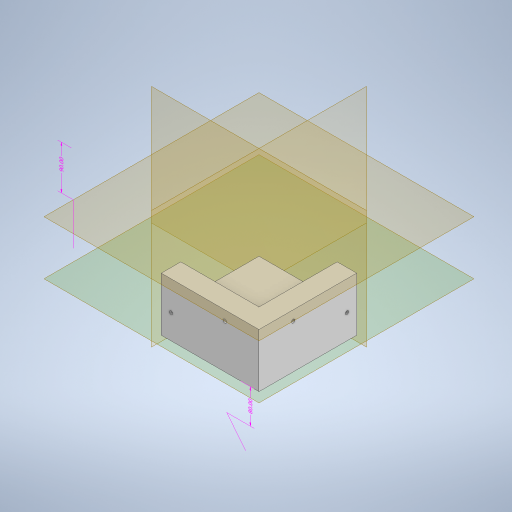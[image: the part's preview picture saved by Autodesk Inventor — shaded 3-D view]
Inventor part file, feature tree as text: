
AUTODESK INVENTOR PART (.ipt)
format: ipt  version: 2023 (Build 270158000, 158)  size: 429,568 bytes
history: native  units: mm
features: sketch x9, extrude x5, other x4, hole x4, plane x4, split x4
ambient origin geometry x8: Origin, YZ Plane, XZ Plane, XY Plane, X Axis, Y Axis, Z Axis, Center Point
bodies: Body1 (feature_tree)
feature tree (30):
  other  "Sólido1"
  other  "Anotaciones"
  extrude  "Extrusión1"  Depth=200.0mm
  hole  "Agujero1"  [1 undecoded]
  extrude  "Extrusión2"  Depth=15.0mm
  extrude  "Extrusión3"  Depth=80.0mm TaperAngle=0.0deg
  extrude  "Extrusión4"  Depth=200.0mm
  extrude  "Extrusión5"  Depth=20.0mm
  hole  "Agujero2"  [1 undecoded]
  plane  "Plano de trabajo1"
  split  "Dividir1"
  plane  "Plano de trabajo2"
  plane  "Plano de trabajo3"
  sketch  "Boceto9"  dims[d37=20.0mm d38=20.0mm]
  plane  "Plano de trabajo4"
  hole  "Agujero3"  [1 undecoded]
  hole  "Agujero4"  [1 undecoded]
  split  "Dividir2"
  split  "Dividir3"
  split  "Dividir4"
  sketch  "Boceto2"  dims[d7=15.0mm d8=200.0mm]
  sketch  "Boceto3"  dims[d9=10.0mm d10=0.0mm]
  sketch  "Boceto4"  dims[d12=1.75mm d13=1.75mm d14=1.75mm d15=1.75mm d16=10.0mm d17=10.0mm d19=30.0mm]
  sketch  "Boceto5"  dims[d20=3.5mm d21=6.0mm d22=4.0mm d23=2.0mm d24=90.0deg d25=8.0mm d26=20.594885mm d27=15.0mm]
  sketch  "Boceto6"  dims[d28=20.0mm d29=80.0mm d30=0.0mm]
  sketch  "Boceto7"  dims[d31=48.0mm d32=200.0mm]
  sketch  "Boceto8"  dims[d33=110.0mm d34=0.0mm d36=20.0mm]
  sketch  "Boceto10"  dims[d39=90.0mm d40=0.0mm d42=10.0mm d43=30.0mm d44=0.0mm d46=1.75mm d47=1.75mm d48=1.75mm d49=1.75mm d50=10.0mm d51=10.0mm d52=15.0mm d56=3.5mm d57=6.0mm d58=4.0mm d59=2.0mm d60=90.0deg d61=8.0mm d62=20.594885mm d63=10.0mm d65=10.0mm d66=10.0mm d67=31.75mm d70=15.0mm d74=200.0mm d78=20.0mm d82=90.0deg d83=10.0mm d84=30.0mm d85=5.0mm d86=5.0mm d87=5.0mm d88=5.0mm d89=20.0mm d91=30.0mm d92=5.0mm d93=5.0mm d94=3.5mm d95=5.0mm d96=5.0mm d97=5.0mm d98=5.0mm d99=5.0mm d100=20.0mm d101=3.5mm d102=6.0mm d103=4.0mm d104=2.0mm d105=90.0deg d106=8.0mm d107=20.594885mm d108=10.0mm d109=30.0mm d110=5.0mm d111=5.0mm d112=5.0mm d113=5.0mm d114=5.0mm d115=5.0mm d116=3.5mm d117=5.0mm d118=5.0mm d119=5.0mm d120=5.0mm d121=5.0mm d122=30.0mm d123=30.0mm d124=3.5mm d125=6.0mm d126=4.0mm d127=2.0mm d128=90.0deg d129=8.0mm d130=20.594885mm d75=1.454734mm d76=6.982969mm d77=80.0mm d79=4.097996mm d80=1.406125mm d81=90.0mm]
  other  "Cota lineal 2"
  other  "Cota lineal 3"
note: 4 required parameter values undecoded (feature->parameter linkage not recoverable at this tier; creation-order binding heuristic only, values carry confidence <= 0.55)
